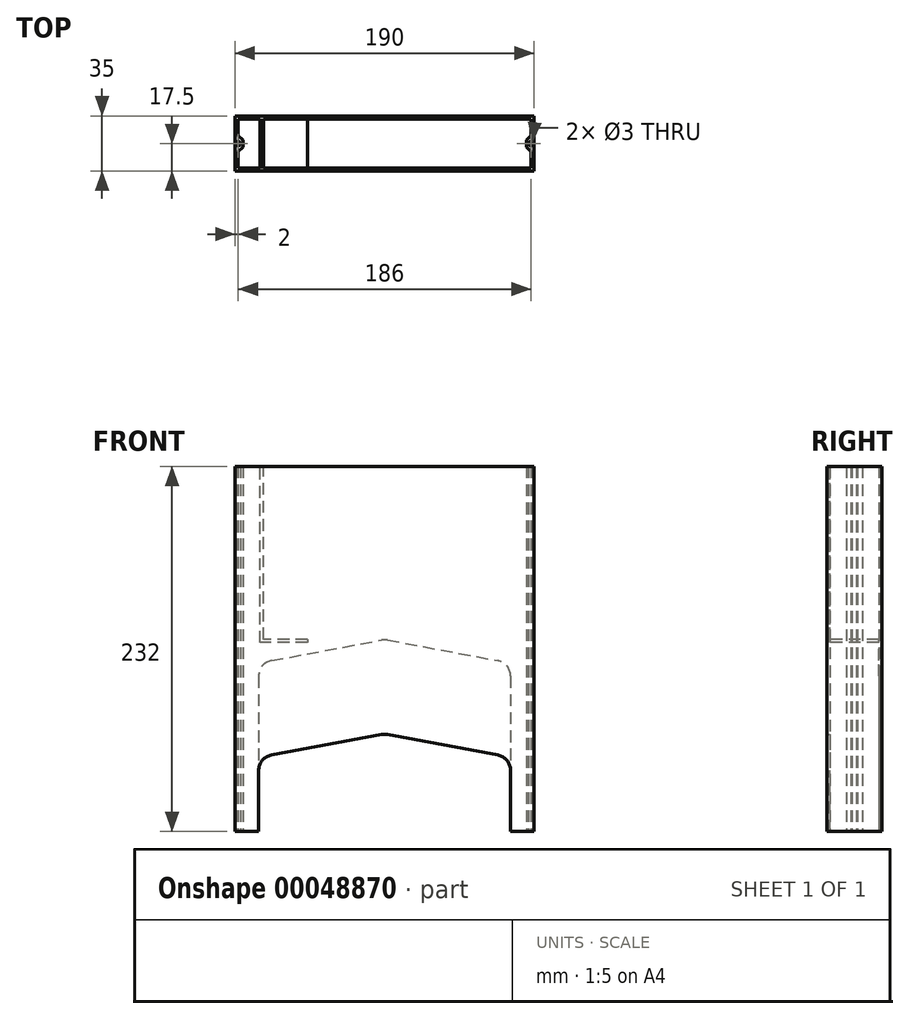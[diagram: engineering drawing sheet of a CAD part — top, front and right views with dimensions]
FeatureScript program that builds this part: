
annotation { "Feature Type Name" : "Feature", "Feature Type Description" : "" }
export const myFeature = defineFeature(function(context is Context, id is Id, definition is map)
    precondition{}
    {
        {
            var Q0;
            Q0=qCreatedBy(makeId("Top.planeOp"),FACE);
            var sketch = newSketch(context, id + "F0", { "sketchPlane" : qUnion([Q0])});
            skLineSegment(sketch, "E0.bottom", {"start": v(0, 0) * mm, "end": v(190, 0) * mm});
            skLineSegment(sketch, "E0.top", {"start": v(0, 35) * mm, "end": v(190, 35) * mm});
            skLineSegment(sketch, "E0.left", {"start": v(0, 0) * mm, "end": v(0, 35) * mm});
            skLineSegment(sketch, "E0.right", {"start": v(190, 0) * mm, "end": v(190, 35) * mm});
            skLineSegment(sketch, "E1.bottom", {"start": v(2, 2) * mm, "end": v(188, 2) * mm});
            skLineSegment(sketch, "E1.top", {"start": v(2, 33) * mm, "end": v(188, 33) * mm});
            skLineSegment(sketch, "E2", {"start": v(2, 33) * mm, "end": v(2, 22.62) * mm});
            skLineSegment(sketch, "E3", {"start": v(2, 22.62) * mm, "end": v(5, 19.62) * mm});
            skLineSegment(sketch, "E4", {"start": v(5, 19.62) * mm, "end": v(5, 15.38) * mm});
            skLineSegment(sketch, "E5", {"start": v(5, 15.38) * mm, "end": v(2, 12.38) * mm});
            skLineSegment(sketch, "E6", {"start": v(2, 12.38) * mm, "end": v(2, 2) * mm});
            skLineSegment(sketch, "E7", {"start": v(2, 22.62) * mm, "end": v(2, 12.38) * mm, "construction": true});
            skCircle(sketch, "E8", {"center": v(2, 17.5) * mm, "radius": 1.5 * mm});
            skLineSegment(sketch, "E9", {"start": v(95, 33) * mm, "end": v(95, 2) * mm, "construction": true});
            skLineSegment(sketch, "E10.MirrorCS", {"start": v(188, 12.38) * mm, "end": v(188, 2) * mm});
            skLineSegment(sketch, "E11.MirrorCS", {"start": v(185, 15.38) * mm, "end": v(188, 12.38) * mm});
            skLineSegment(sketch, "E12.MirrorCS", {"start": v(185, 19.62) * mm, "end": v(185, 15.38) * mm});
            skCircle(sketch, "E13.MirrorC", {"center": v(188, 17.5) * mm, "radius": 1.5 * mm});
            skLineSegment(sketch, "E14.MirrorCS", {"start": v(188, 33) * mm, "end": v(188, 22.62) * mm});
            skLineSegment(sketch, "E15.MirrorCS", {"start": v(188, 22.62) * mm, "end": v(185, 19.62) * mm});
            skSolve(sketch);
        }
        {
            var Q0;
            Q0=makeQuery(id+"F0.imprint","IMPRINT",FACE,{"disambiguationData":[TD([[makeQuery(id+"F0.imprint","IMPRINT",EDGE,{"derivedFrom":sQuery(id+"F0.wireOp",EDGE,"E0.bottom")}),1.0]])]});
            extrude(context, id + "F1", {"entities" : qUnion([Q0]), "depth" : 232 * mm});
        }
        {
            var Q0;
            Q0=makeQuery(id+"F1.opExtrude","SWEPT_FACE",FACE,{"disambiguationData":[OSD([sQuery(id+"F0.wireOp",EDGE,"E0.bottom")])]});
            var sketch = newSketch(context, id + "F2", { "sketchPlane" : qUnion([Q0])});
            skLineSegment(sketch, "E16.bottom", {"start": v(16, 232) * mm, "end": v(18, 232) * mm});
            skLineSegment(sketch, "E16.top", {"start": v(16, 120) * mm, "end": v(18, 120) * mm});
            skLineSegment(sketch, "E16.left", {"start": v(16, 232) * mm, "end": v(16, 120) * mm});
            skLineSegment(sketch, "E16.right", {"start": v(18, 232) * mm, "end": v(18, 120) * mm});
            skLineSegment(sketch, "E17.bottom", {"start": v(16, 120) * mm, "end": v(46, 120) * mm});
            skLineSegment(sketch, "E17.top", {"start": v(16, 122) * mm, "end": v(46, 122) * mm});
            skLineSegment(sketch, "E17.left", {"start": v(16, 120) * mm, "end": v(16, 122) * mm});
            skLineSegment(sketch, "E17.right", {"start": v(46, 120) * mm, "end": v(46, 122) * mm});
            skSolve(sketch);
        }
        {
            var Q0;
            Q0=qSketchRegion(id+"F2",true);
            extrude(context, id + "F3", {"entities" : qUnion([Q0]), "operationType" : NewBodyOperationType.ADD, "oppositeDirection" : true, "depth" : 33 * mm});
        }
        {
            var Q0;
            Q0=makeQuery(id+"F1.opExtrude","SWEPT_FACE",FACE,{"disambiguationData":[OSD([sQuery(id+"F0.wireOp",EDGE,"E0.top")])]});
            var sketch = newSketch(context, id + "F4", { "sketchPlane" : qUnion([Q0])});
            skLineSegment(sketch, "E18.bottom", {"start": v(-15, 107) * mm, "end": v(-175, 107) * mm});
            skLineSegment(sketch, "E18.top", {"start": v(-15, 0) * mm, "end": v(-175, 0) * mm});
            skLineSegment(sketch, "E18.left", {"start": v(-15, 107) * mm, "end": v(-15, 0) * mm});
            skLineSegment(sketch, "E18.right", {"start": v(-175, 107) * mm, "end": v(-175, 0) * mm});
            skLineSegment(sketch, "E19", {"start": v(-15, 107) * mm, "end": v(-95, 122) * mm});
            skLineSegment(sketch, "E20", {"start": v(-95, 122) * mm, "end": v(-175, 107) * mm});
            skSolve(sketch);
        }
        {
            var Q0;
            Q0=qSketchRegion(id+"F4",true);
            extrude(context, id + "F5", {"entities" : qUnion([Q0]), "operationType" : NewBodyOperationType.REMOVE, "oppositeDirection" : true, "depth" : 5 * mm});
        }
        {
            var Q0;
            Q0=makeQuery(id+"F1.opExtrude","SWEPT_FACE",FACE,{"disambiguationData":[OSD([sQuery(id+"F0.wireOp",EDGE,"E0.bottom")])]});
            var sketch = newSketch(context, id + "F6", { "sketchPlane" : qUnion([Q0])});
            skLineSegment(sketch, "E21.bottom", {"start": v(15, 47) * mm, "end": v(175, 47) * mm});
            skLineSegment(sketch, "E21.top", {"start": v(15, 0) * mm, "end": v(175, 0) * mm});
            skLineSegment(sketch, "E21.left", {"start": v(15, 47) * mm, "end": v(15, 0) * mm});
            skLineSegment(sketch, "E21.right", {"start": v(175, 47) * mm, "end": v(175, 0) * mm});
            skLineSegment(sketch, "E22", {"start": v(175, 47) * mm, "end": v(95, 62) * mm});
            skLineSegment(sketch, "E23", {"start": v(95, 62) * mm, "end": v(15, 47) * mm});
            skSolve(sketch);
        }
        {
            var Q0;
            Q0 = qSketchRegion(id + "F6", true);
            extrude(context, id + "F7", {"entities" : qUnion([Q0]), "operationType" : NewBodyOperationType.REMOVE, "oppositeDirection" : true, "depth" : 5 * mm});
        }
        {
            var Q0;
            Q0=makeQuery(id+"F7.boolean.opBoolean","COPY",EDGE,{"derivedFrom":makeQuery(id+"F7.opExtrude","SWEPT_EDGE",EDGE,{"disambiguationData":[OSD([sQuery(id+"F6.wireOp",EDGE,"E21.bottom"),sQuery(id+"F6.wireOp",EDGE,"E21.right"),sQuery(id+"F6.wireOp",EDGE,"32699f41-bd31-492c-929e-7ffe1c4d67b9")])]})});
            var Q1;
            Q1=makeQuery(id+"F5.boolean.opBoolean","COPY",EDGE,{"derivedFrom":makeQuery(id+"F5.opExtrude","SWEPT_EDGE",EDGE,{"disambiguationData":[OSD([sQuery(id+"F4.wireOp",EDGE,"E18.bottom"),sQuery(id+"F4.wireOp",EDGE,"E18.right"),sQuery(id+"F4.wireOp",EDGE,"c84e8199-388f-4f57-a25a-67814fa04226")])]})});
            var Q2;
            Q2=makeQuery(id+"F5.boolean.opBoolean","COPY",EDGE,{"derivedFrom":makeQuery(id+"F5.opExtrude","SWEPT_EDGE",EDGE,{"disambiguationData":[OSD([sQuery(id+"F4.wireOp",EDGE,"E18.bottom"),sQuery(id+"F4.wireOp",EDGE,"E18.left"),sQuery(id+"F4.wireOp",EDGE,"c84e8199-388f-4f57-a25a-67814fa04226")])]})});
            var Q3;
            Q3=makeQuery(id+"F7.boolean.opBoolean","COPY",EDGE,{"derivedFrom":makeQuery(id+"F7.opExtrude","SWEPT_EDGE",EDGE,{"disambiguationData":[OSD([sQuery(id+"F6.wireOp",EDGE,"E21.bottom"),sQuery(id+"F6.wireOp",EDGE,"E21.left"),sQuery(id+"F6.wireOp",EDGE,"32699f41-bd31-492c-929e-7ffe1c4d67b9")])]})});
            var Q4;
            Q4=makeQuery(id+"F5.boolean.opBoolean","COPY",EDGE,{"derivedFrom":makeQuery(id+"F5.opExtrude","SWEPT_EDGE",EDGE,{"disambiguationData":[OSD([sQuery(id+"F4.wireOp",EDGE,"E19"),sQuery(id+"F4.wireOp",EDGE,"E20")])]})});
            var Q5;
            Q5=makeQuery(id+"F7.boolean.opBoolean","COPY",EDGE,{"derivedFrom":makeQuery(id+"F7.opExtrude","SWEPT_EDGE",EDGE,{"disambiguationData":[OSD([sQuery(id+"F6.wireOp",EDGE,"E22"),sQuery(id+"F6.wireOp",EDGE,"E23")])]})});
            fillet(context, id + "F8", {"entities" : qUnion([Q0, Q1, Q2, Q3, Q4, Q5]), "radius" : 10 * mm, "tangentPropagation" : true, "allowEdgeOverflow" : false});
        }
    });
